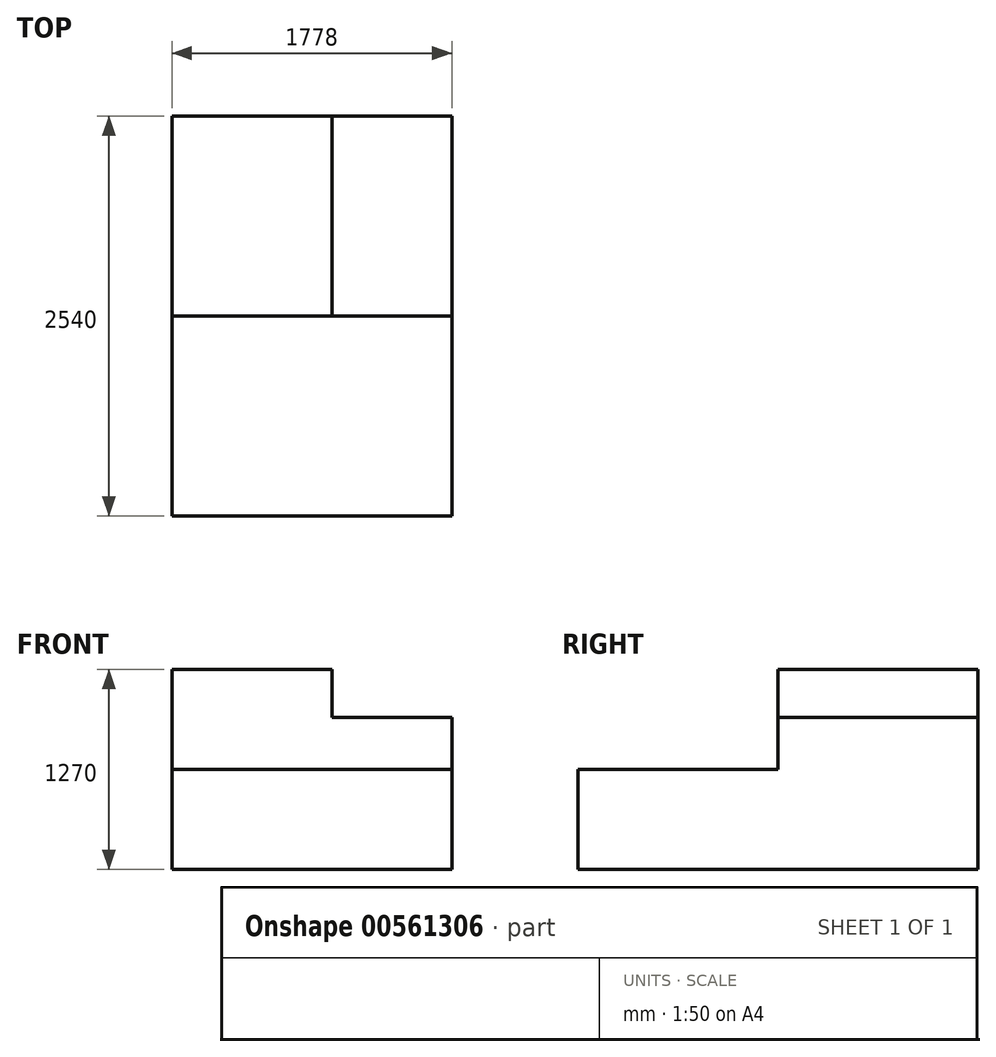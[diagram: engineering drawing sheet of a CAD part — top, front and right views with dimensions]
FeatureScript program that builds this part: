
annotation { "Feature Type Name" : "Feature", "Feature Type Description" : "" }
export const myFeature = defineFeature(function(context is Context, id is Id, definition is map)
    precondition{}
    {
        {
            var Q0;
            Q0=qCreatedBy(makeId("Right.planeOp"),FACE);
            var sketch = newSketch(context, id + "F0", { "sketchPlane" : qUnion([Q0])});
            skLineSegment(sketch, "E0.bottom", {"start": v(2448, -75.72) * mm, "end": v(-92, -75.72) * mm});
            skLineSegment(sketch, "E0.top", {"start": v(2448, 1194.28) * mm, "end": v(-92, 1194.28) * mm});
            skLineSegment(sketch, "E0.left", {"start": v(2448, -75.72) * mm, "end": v(2448, 1194.28) * mm});
            skLineSegment(sketch, "E0.right", {"start": v(-92, -75.72) * mm, "end": v(-92, 1194.28) * mm});
            skSolve(sketch);
        }
        {
            var Q0;
            Q0 = qSketchRegion(id + "F0", true);
            extrude(context, id + "F1", {"entities" : qUnion([Q0]), "depth" : 1778 * mm, "offsetDistance" : 25.4 * mm});
        }
        {
            var Q0;
            Q0=makeQuery(id+"F1.opExtrude","CAP_FACE",FACE,{"disambiguationData":[OSD([sQuery(id+"F0.wireOp",EDGE,"E0.bottom"),sQuery(id+"F0.wireOp",EDGE,"E0.top"),sQuery(id+"F0.wireOp",EDGE,"E0.left"),sQuery(id+"F0.wireOp",EDGE,"E0.right")])],"isStart":false});
            var sketch = newSketch(context, id + "F2", { "sketchPlane" : qUnion([Q0])});
            skLineSegment(sketch, "E1", {"start": v(-92, -75.72) * mm, "end": v(-92, 559.28) * mm});
            skLineSegment(sketch, "E2", {"start": v(-92, 559.28) * mm, "end": v(1178, 559.28) * mm});
            skLineSegment(sketch, "E3", {"start": v(1178, 559.28) * mm, "end": v(1178, 1194.28) * mm});
            skSolve(sketch);
        }
        {
            var Q0;
            {var subQ0=sQuery(id+"F2.wireOp",EDGE,"E2");Q0=makeQuery(id+"F2.imprint","IMPRINT",FACE,{"disambiguationData":[TD([[makeQuery(id+"F2.imprint","IMPRINT",EDGE,{"derivedFrom":subQ0}),1.0]])]});}
            extrude(context, id + "F3", {"entities" : qUnion([Q0]), "operationType" : NewBodyOperationType.REMOVE, "endBound" : BoundingType.THROUGH_ALL, "oppositeDirection" : true, "depth" : 25.4 * mm, "offsetDistance" : 25.4 * mm});
        }
        {
            var Q0;
            Q0=makeQuery(id+"F3.boolean.opBoolean","COPY",FACE,{"derivedFrom":makeQuery(id+"F3.opExtrude","SWEPT_FACE",FACE,{"disambiguationData":[OSD([sQuery(id+"F2.wireOp",EDGE,"E3")])]})});
            var sketch = newSketch(context, id + "F4", { "sketchPlane" : qUnion([Q0])});
            skLineSegment(sketch, "E4", {"start": v(1778, 1194.28) * mm, "end": v(1016, 1194.28) * mm});
            skLineSegment(sketch, "E5", {"start": v(1016, 1194.28) * mm, "end": v(1016, 889.48) * mm});
            skLineSegment(sketch, "E6", {"start": v(1016, 889.48) * mm, "end": v(1778, 889.48) * mm});
            skSolve(sketch);
        }
        {
            var Q0;
            {var subQ0=sQuery(id+"F4.wireOp",EDGE,"E4");Q0=makeQuery(id+"F4.imprint","IMPRINT",FACE,{"disambiguationData":[TD([[makeQuery(id+"F4.imprint","IMPRINT",EDGE,{"derivedFrom":subQ0}),-1.0]])]});}
            extrude(context, id + "F5", {"entities" : qUnion([Q0]), "operationType" : NewBodyOperationType.REMOVE, "endBound" : BoundingType.THROUGH_ALL, "oppositeDirection" : true, "depth" : 25.4 * mm, "offsetDistance" : 25.4 * mm});
        }
    });
